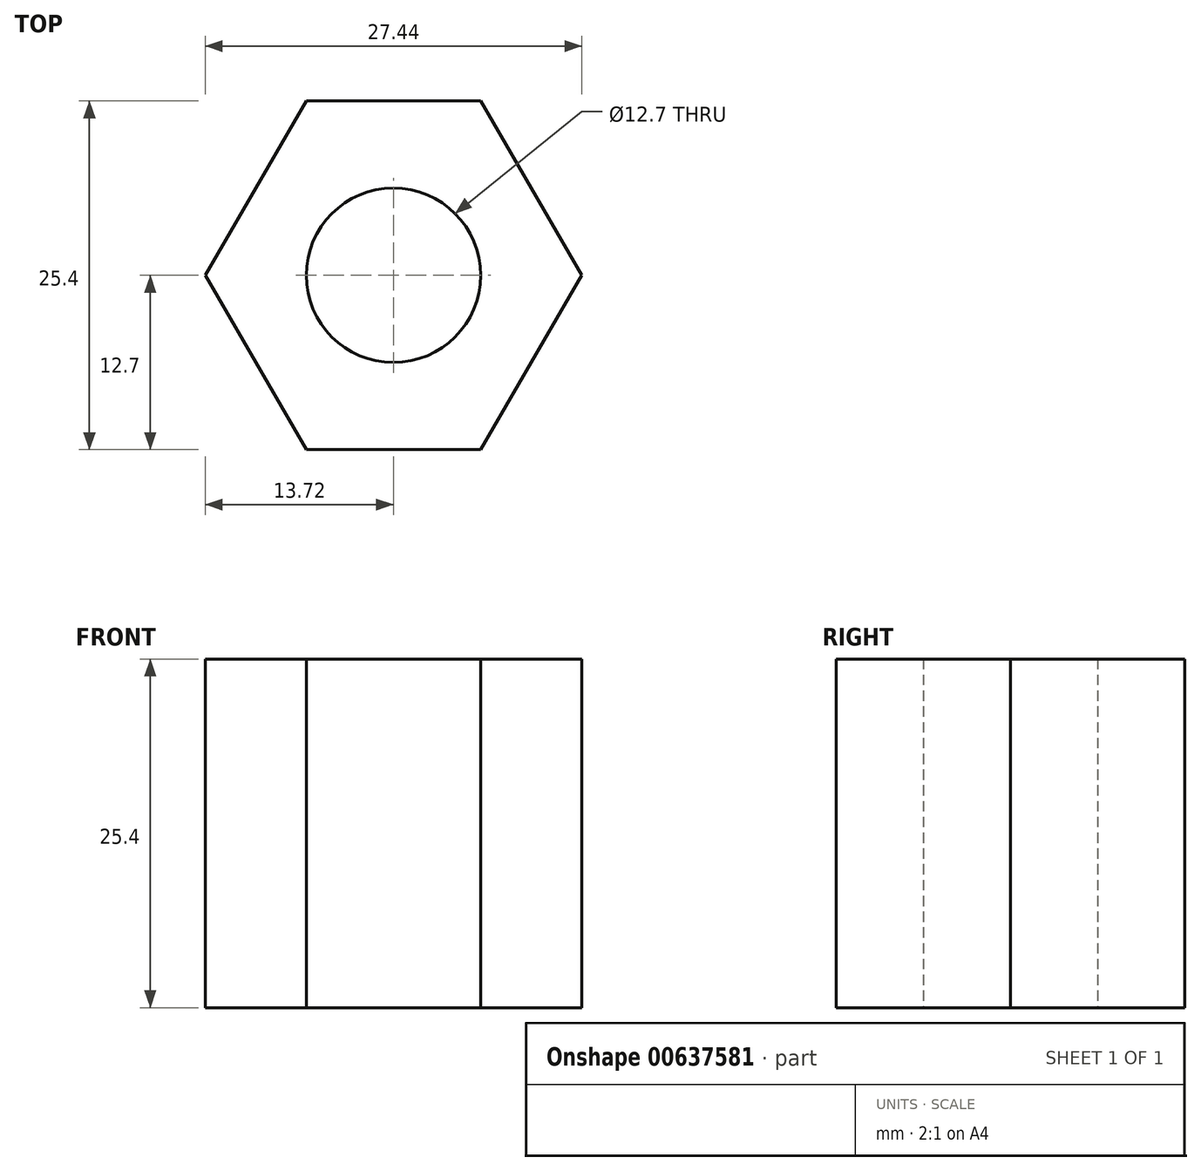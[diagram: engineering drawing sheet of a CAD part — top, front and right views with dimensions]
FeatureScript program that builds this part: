
annotation { "Feature Type Name" : "Feature", "Feature Type Description" : "" }
export const myFeature = defineFeature(function(context is Context, id is Id, definition is map)
    precondition{}
    {
        {
            var Q0;
            Q0=qCreatedBy(makeId("Top.planeOp"),FACE);
            var sketch = newSketch(context, id + "F0", { "sketchPlane" : qUnion([Q0])});
            skLineSegment(sketch, "E0", {"start": v(0, 0) * mm, "end": v(0, 12.7) * mm});
            skLineSegment(sketch, "E1", {"start": v(0, 12.7) * mm, "end": v(0, 0) * mm});
            skLineSegment(sketch, "E2", {"start": v(0, -12.7) * mm, "end": v(0, 0) * mm});
            skLineSegment(sketch, "E3", {"start": v(0, 12.7) * mm, "end": v(6.35, 12.7) * mm});
            skLineSegment(sketch, "E4", {"start": v(0, 12.7) * mm, "end": v(-6.35, 12.7) * mm});
            skLineSegment(sketch, "E5", {"start": v(0, -12.7) * mm, "end": v(6.35, -12.7) * mm});
            skLineSegment(sketch, "E6", {"start": v(0, -12.7) * mm, "end": v(-6.35, -12.7) * mm});
            skLineSegment(sketch, "E7", {"start": v(-6.35, -12.7) * mm, "end": v(-13.72, 0) * mm});
            skLineSegment(sketch, "E8", {"start": v(-6.35, 12.7) * mm, "end": v(-13.72, 0) * mm});
            skLineSegment(sketch, "E9", {"start": v(6.35, 12.7) * mm, "end": v(13.72, 0) * mm});
            skLineSegment(sketch, "E10", {"start": v(13.72, 0) * mm, "end": v(6.35, -12.7) * mm});
            skCircle(sketch, "E11", {"center": v(0, 0) * mm, "radius": 6.35 * mm});
            skSolve(sketch);
        }
        {
            var Q0;
            Q0 = qSketchRegion(id + "F0", true);
            extrude(context, id + "F1", {"entities" : qUnion([Q0]), "depth" : 25.4 * mm, "offsetDistance" : 25.4 * mm});
        }
    });
